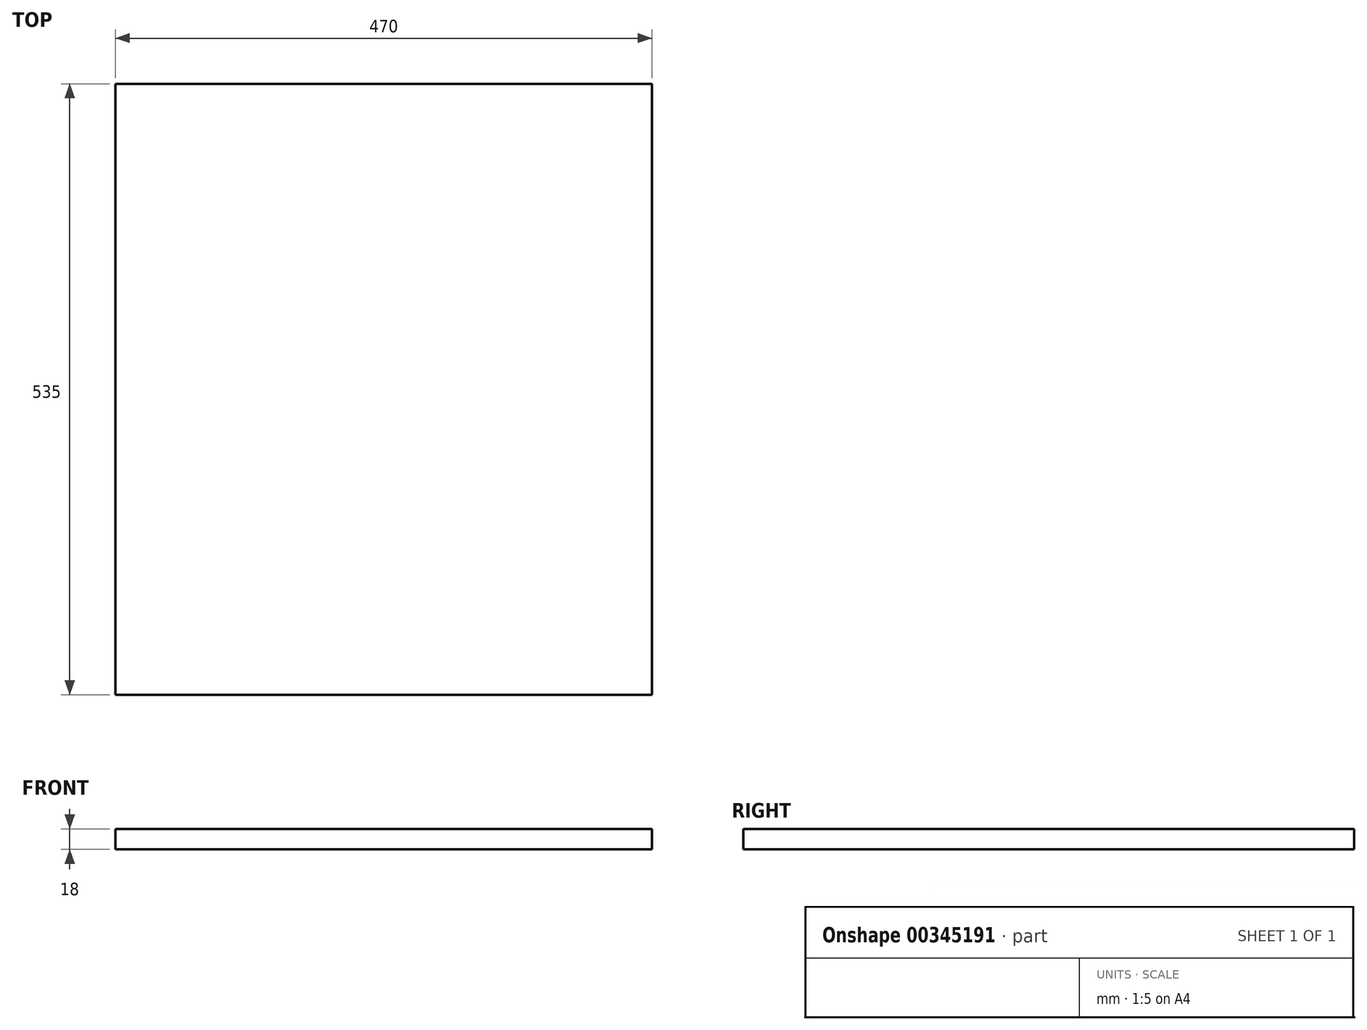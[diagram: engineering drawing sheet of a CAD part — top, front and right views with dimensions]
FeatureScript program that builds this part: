
annotation { "Feature Type Name" : "Feature", "Feature Type Description" : "" }
export const myFeature = defineFeature(function(context is Context, id is Id, definition is map)
    precondition{}
    {
        {
            var Q0;
            Q0=qCreatedBy(makeId("Top.planeOp"),FACE);
            var sketch = newSketch(context, id + "F0", { "sketchPlane" : qUnion([Q0])});
            skLineSegment(sketch, "E0", {"start": v(0, 0) * mm, "end": v(0, 535) * mm});
            skLineSegment(sketch, "E1", {"start": v(0, 535) * mm, "end": v(470, 535) * mm});
            skLineSegment(sketch, "E2", {"start": v(470, 535) * mm, "end": v(470, 0) * mm});
            skLineSegment(sketch, "E3", {"start": v(470, 0) * mm, "end": v(0, 0) * mm});
            skSolve(sketch);
        }
        {
            var Q0;
            Q0=makeQuery(id+"F0.imprint","IMPRINT",FACE,{"disambiguationData":[TD([[makeQuery(id+"F0.imprint","IMPRINT",EDGE,{"derivedFrom":sQuery(id+"F0.wireOp",EDGE,"E0")}),-1.0]])]});
            extrude(context, id + "F1", {"entities" : qUnion([Q0]), "depth" : 18 * mm});
        }
    });
